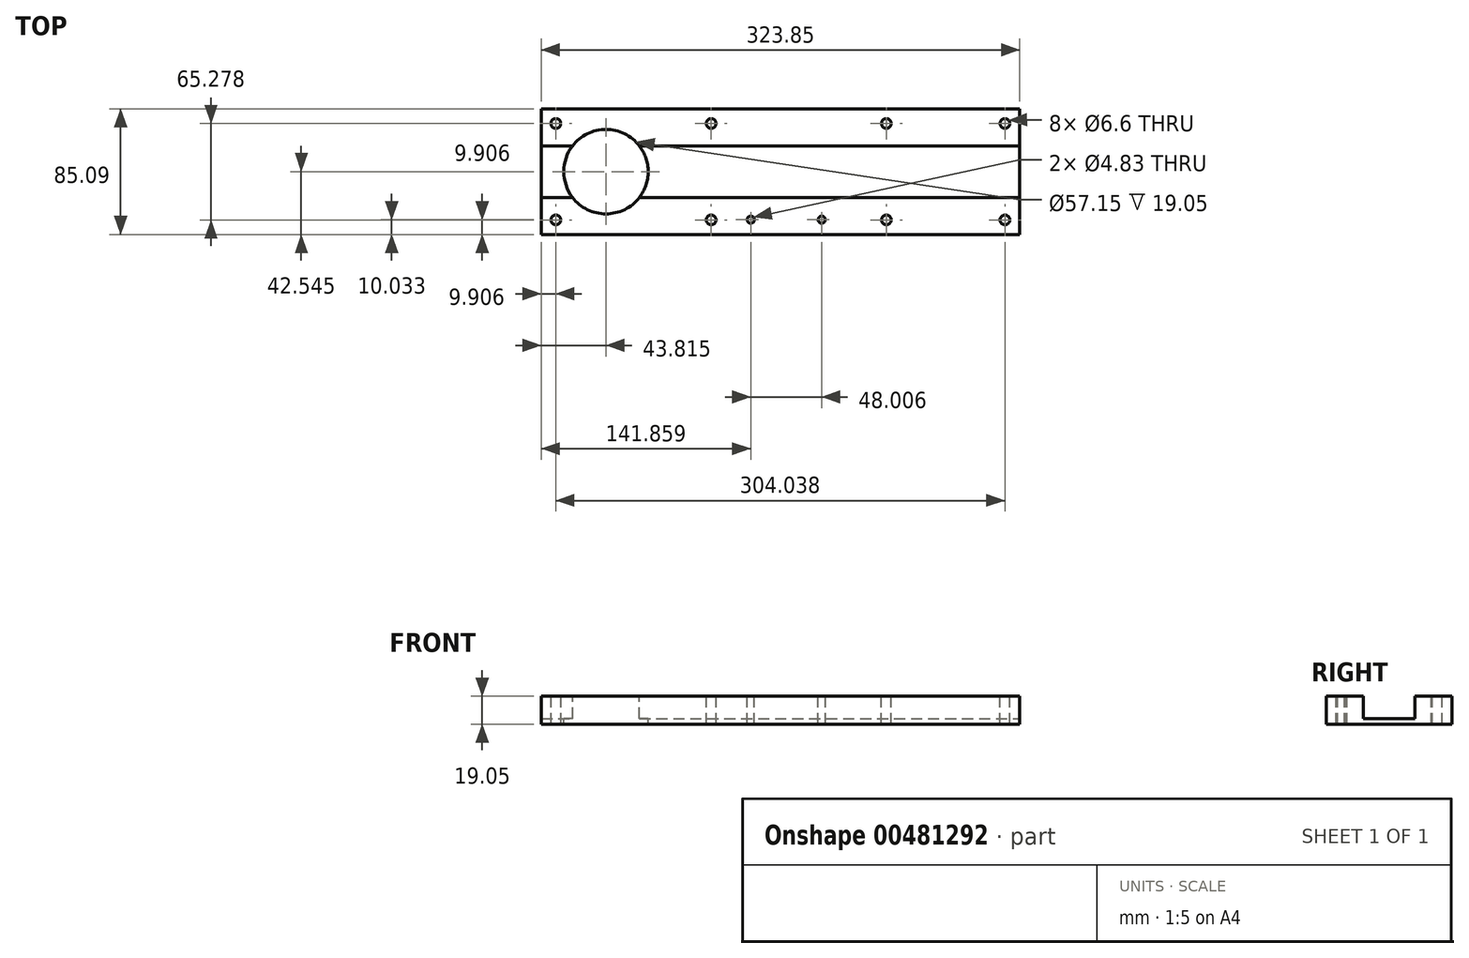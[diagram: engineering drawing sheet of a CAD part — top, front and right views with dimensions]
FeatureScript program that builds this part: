
annotation { "Feature Type Name" : "Feature", "Feature Type Description" : "" }
export const myFeature = defineFeature(function(context is Context, id is Id, definition is map)
    precondition{}
    {
        {
            var Q0;
            Q0=qCreatedBy(makeId("Top.planeOp"),FACE);
            var sketch = newSketch(context, id + "F0", { "sketchPlane" : qUnion([Q0])});
            skLineSegment(sketch, "E0.bottom", {"start": v(0, 85.09) * mm, "end": v(323.85, 85.09) * mm});
            skLineSegment(sketch, "E0.top", {"start": v(0, 0) * mm, "end": v(323.85, 0) * mm});
            skLineSegment(sketch, "E0.left", {"start": v(0, 85.09) * mm, "end": v(0, 0) * mm});
            skLineSegment(sketch, "E0.right", {"start": v(323.85, 85.09) * mm, "end": v(323.85, 0) * mm});
            skSolve(sketch);
        }
        {
            var Q0;
            Q0 = qSketchRegion(id + "F0", true);
            extrude(context, id + "F1", {"entities" : qUnion([Q0]), "depth" : 19.05 * mm});
        }
        {
            var Q0;
            Q0=makeQuery(id+"F1.opExtrude","CAP_FACE",FACE,{"disambiguationData":[OSD([sQuery(id+"F0.wireOp",EDGE,"E0.bottom"),sQuery(id+"F0.wireOp",EDGE,"E0.top"),sQuery(id+"F0.wireOp",EDGE,"E0.left"),sQuery(id+"F0.wireOp",EDGE,"E0.right")])],"isStart":false});
            var sketch = newSketch(context, id + "F2", { "sketchPlane" : qUnion([Q0])});
            skCircle(sketch, "E1", {"center": v(43.82, 42.54) * mm, "radius": 22.6 * mm, "construction": true});
            skLineSegment(sketch, "E2.0", {"start": v(0, 85.09) * mm, "end": v(0, 0) * mm, "construction": true});
            skLineSegment(sketch, "E3", {"start": v(0, 42.54) * mm, "end": v(162.46, 42.54) * mm, "construction": true});
            skLineSegment(sketch, "E4", {"start": v(21.2, 10.66) * mm, "end": v(21.2, 107.9) * mm, "construction": true});
            skCircle(sketch, "E5", {"center": v(43.82, 42.54) * mm, "radius": 28.58 * mm});
            skSolve(sketch);
        }
        {
            var Q0;
            Q0 = qSketchRegion(id + "F2", true);
            extrude(context, id + "F3", {"entities" : qUnion([Q0]), "operationType" : NewBodyOperationType.REMOVE, "endBound" : BoundingType.THROUGH_ALL, "oppositeDirection" : true, "depth" : 25.4 * mm});
        }
        {
            var Q0;
            Q0=makeQuery(id+"F1.opExtrude","CAP_FACE",FACE,{"disambiguationData":[OSD([sQuery(id+"F0.wireOp",EDGE,"E0.bottom"),sQuery(id+"F0.wireOp",EDGE,"E0.top"),sQuery(id+"F0.wireOp",EDGE,"E0.left"),sQuery(id+"F0.wireOp",EDGE,"E0.right")])],"isStart":false});
            var sketch = newSketch(context, id + "F4", { "sketchPlane" : qUnion([Q0])});
            skLineSegment(sketch, "E6.0", {"start": v(0, 85.09) * mm, "end": v(323.85, 85.09) * mm, "construction": true});
            skLineSegment(sketch, "E7", {"start": v(0, 78.49) * mm, "end": v(323.85, 78.49) * mm, "construction": true});
            skCircle(sketch, "E8", {"center": v(9.9, 75.18) * mm, "radius": 3.3 * mm});
            skCircle(sketch, "E9", {"center": v(115.06, 75.18) * mm, "radius": 3.3 * mm});
            skCircle(sketch, "E10", {"center": v(233.68, 75.18) * mm, "radius": 3.3 * mm});
            skCircle(sketch, "E11", {"center": v(313.94, 75.18) * mm, "radius": 3.3 * mm});
            skLineSegment(sketch, "E12", {"start": v(6.6, 56.84) * mm, "end": v(6.6, 100.8) * mm, "construction": true});
            skLineSegment(sketch, "E13", {"start": v(111.76, 71.19) * mm, "end": v(111.76, 107.6) * mm, "construction": true});
            skLineSegment(sketch, "E14", {"start": v(317.25, 60.73) * mm, "end": v(317.25, 95.81) * mm, "construction": true});
            skLineSegment(sketch, "E15", {"start": v(236.98, 62.07) * mm, "end": v(236.98, 116.24) * mm, "construction": true});
            skLineSegment(sketch, "E16", {"start": v(0, 42.54) * mm, "end": v(323.85, 42.54) * mm, "construction": true});
            skCircle(sketch, "E17.MirrorC", {"center": v(115.06, 9.9) * mm, "radius": 3.3 * mm});
            skCircle(sketch, "E18.MirrorC", {"center": v(9.9, 9.9) * mm, "radius": 3.3 * mm});
            skCircle(sketch, "E19.MirrorC", {"center": v(233.68, 9.9) * mm, "radius": 3.3 * mm});
            skCircle(sketch, "E20.MirrorC", {"center": v(313.94, 9.9) * mm, "radius": 3.3 * mm});
            skSolve(sketch);
        }
        {
            var Q0;
            Q0 = qSketchRegion(id + "F4", true);
            extrude(context, id + "F5", {"entities" : qUnion([Q0]), "operationType" : NewBodyOperationType.REMOVE, "endBound" : BoundingType.THROUGH_ALL, "oppositeDirection" : true, "depth" : 25.4 * mm});
        }
        {
            var Q0;
            Q0=makeQuery(id+"F1.opExtrude","CAP_FACE",FACE,{"disambiguationData":[OSD([sQuery(id+"F0.wireOp",EDGE,"E0.bottom"),sQuery(id+"F0.wireOp",EDGE,"E0.top"),sQuery(id+"F0.wireOp",EDGE,"E0.left"),sQuery(id+"F0.wireOp",EDGE,"E0.right")])],"isStart":false});
            var sketch = newSketch(context, id + "F6", { "sketchPlane" : qUnion([Q0])});
            skLineSegment(sketch, "E21.0", {"start": v(0, 0) * mm, "end": v(323.85, 0) * mm, "construction": true});
            skCircle(sketch, "E22", {"center": v(141.86, 10.03) * mm, "radius": 2.41 * mm});
            skCircle(sketch, "E23", {"center": v(189.87, 10.03) * mm, "radius": 2.41 * mm});
            skLineSegment(sketch, "E24", {"start": v(192.28, 31.45) * mm, "end": v(192.28, 56.58) * mm, "construction": true});
            skLineSegment(sketch, "E25", {"start": v(144.27, 19.26) * mm, "end": v(144.27, 3.48) * mm, "construction": true});
            skLineSegment(sketch, "E26", {"start": v(187.45, 20.57) * mm, "end": v(187.45, -4.74) * mm, "construction": true});
            skLineSegment(sketch, "E27", {"start": v(141.86, 7.62) * mm, "end": v(205.37, 7.62) * mm, "construction": true});
            skSolve(sketch);
        }
        {
            var Q0;
            Q0 = qSketchRegion(id + "F6", true);
            extrude(context, id + "F7", {"entities" : qUnion([Q0]), "operationType" : NewBodyOperationType.REMOVE, "endBound" : BoundingType.THROUGH_ALL, "oppositeDirection" : true, "depth" : 25.4 * mm});
        }
        {
            var Q0;
            Q0=makeQuery(id+"F1.opExtrude","CAP_FACE",FACE,{"disambiguationData":[OSD([sQuery(id+"F0.wireOp",EDGE,"E0.bottom"),sQuery(id+"F0.wireOp",EDGE,"E0.top"),sQuery(id+"F0.wireOp",EDGE,"E0.left"),sQuery(id+"F0.wireOp",EDGE,"E0.right")])],"isStart":false});
            var sketch = newSketch(context, id + "F8", { "sketchPlane" : qUnion([Q0])});
            skLineSegment(sketch, "E28", {"start": v(0, 42.54) * mm, "end": v(323.85, 42.54) * mm, "construction": true});
            skLineSegment(sketch, "E29.bottom", {"start": v(0, 60) * mm, "end": v(323.85, 60) * mm});
            skLineSegment(sketch, "E29.top", {"start": v(0, 25.08) * mm, "end": v(323.85, 25.08) * mm});
            skLineSegment(sketch, "E29.left", {"start": v(0, 60) * mm, "end": v(0, 25.08) * mm});
            skLineSegment(sketch, "E29.right", {"start": v(323.85, 60) * mm, "end": v(323.85, 25.08) * mm});
            skSolve(sketch);
        }
        {
            var Q0;
            {var subQ0=sQuery(id+"F8.wireOp",EDGE,"E29.right");Q0=makeQuery(id+"F8.imprint","IMPRINT",FACE,{"disambiguationData":[TD([[makeQuery(id+"F8.imprint","IMPRINT",EDGE,{"derivedFrom":subQ0}),-1.0]])]});}
            var Q1;
            {var subQ0=sQuery(id+"F8.wireOp",EDGE,"E29.left");Q1=makeQuery(id+"F8.imprint","IMPRINT",FACE,{"disambiguationData":[TD([[makeQuery(id+"F8.imprint","IMPRINT",EDGE,{"derivedFrom":subQ0}),1.0]])]});}
            extrude(context, id + "F9", {"entities" : qUnion([Q0, Q1]), "operationType" : NewBodyOperationType.REMOVE, "oppositeDirection" : true, "depth" : 15.24 * mm});
        }
    });
